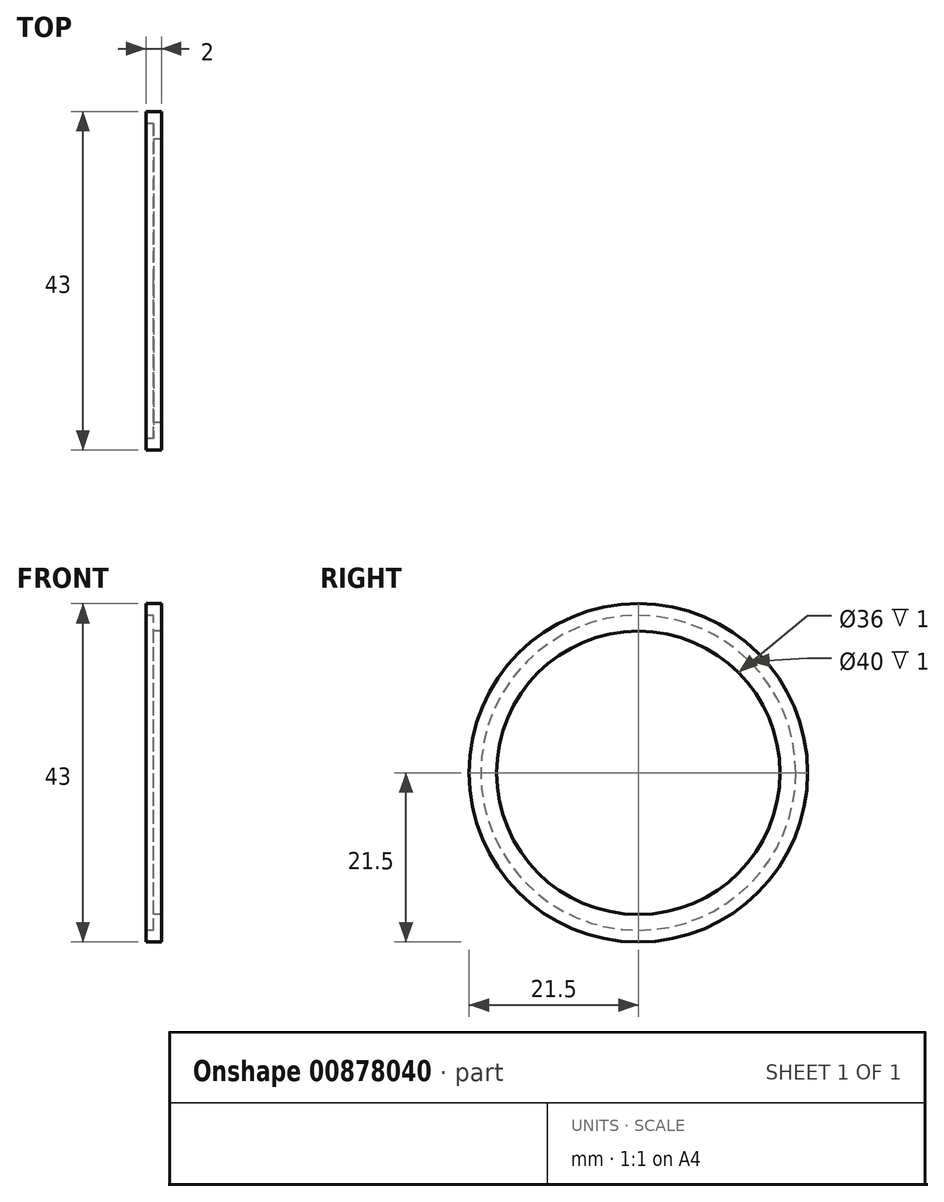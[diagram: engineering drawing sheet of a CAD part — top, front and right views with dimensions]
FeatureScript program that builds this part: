
annotation { "Feature Type Name" : "Feature", "Feature Type Description" : "" }
export const myFeature = defineFeature(function(context is Context, id is Id, definition is map)
    precondition{}
    {
        {
            var Q0;
            Q0=qCreatedBy(makeId("Right.planeOp"),FACE);
            var sketch = newSketch(context, id + "F0", { "sketchPlane" : qUnion([Q0])});
            skCircle(sketch, "E0", {"center": v(0, 0) * mm, "radius": 21.5 * mm});
            skCircle(sketch, "E1", {"center": v(0, 0) * mm, "radius": 18 * mm});
            skSolve(sketch);
        }
        {
            var Q0;
            Q0=makeQuery(id+"F0.imprint","IMPRINT",FACE,{"disambiguationData":[TD([[makeQuery(id+"F0.imprint","IMPRINT",EDGE,{"derivedFrom":sQuery(id+"F0.wireOp",EDGE,"E0")}),1.0]])]});
            extrude(context, id + "F1", {"entities" : qUnion([Q0]), "depth" : 2 * mm, "offsetDistance" : 25 * mm});
        }
        {
            var Q0;
            Q0=qCreatedBy(makeId("Right.planeOp"),FACE);
            var sketch = newSketch(context, id + "F2", { "sketchPlane" : qUnion([Q0])});
            skCircle(sketch, "E2", {"center": v(0, 0) * mm, "radius": 15.7 * mm});
            skCircle(sketch, "E3", {"center": v(0, 0) * mm, "radius": 20 * mm});
            skSolve(sketch);
        }
        {
            var Q0;
            Q0=makeQuery(id+"F2.imprint","IMPRINT",FACE,{"disambiguationData":[TD([[makeQuery(id+"F2.imprint","IMPRINT",EDGE,{"derivedFrom":sQuery(id+"F2.wireOp",EDGE,"E2")}),-1.0]])]});
            extrude(context, id + "F3", {"entities" : qUnion([Q0]), "operationType" : NewBodyOperationType.REMOVE, "depth" : 1 * mm, "offsetDistance" : 25 * mm});
        }
    });
